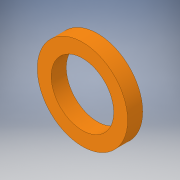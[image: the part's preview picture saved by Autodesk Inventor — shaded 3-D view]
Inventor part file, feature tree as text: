
AUTODESK INVENTOR PART (.ipt)
format: ipt  version: 2017 (Build 210142000, 142)  size: 103,936 bytes
history: native  units: in
note: dims shown in document units (in); Inventor stores cm internally (conversion verified against a paired STEP export)
features: sketch x3, hole x2, extrude x1
ambient origin geometry x8: Origin, YZ Plane, XZ Plane, XY Plane, X Axis, Y Axis, Z Axis, Center Point
bodies: Solid1 (feature_tree)
feature tree (6):
  extrude  "Extrusion1"  Depth=0.125in TaperAngle=0.0deg
  hole  "Hole1"  [1 undecoded]
  hole  "Hole2"  [1 undecoded]
  sketch  "Sketch1"  dims[d0=0.75in d1=0.125in d2=0.0in]
  sketch  "Sketch2"  dims[d3=0.51in d4=0.75in d5=0.375in d6=0.25in d7=0.5635in d8=1.0in d9=0.8108in]
  sketch  "Sketch3"  dims[d10=0.52in d11=0.75in d12=0.375in d13=0.25in d14=0.5635in d15=1.0in d16=0.8108in]
note: 2 required parameter values undecoded (feature->parameter linkage not recoverable at this tier; creation-order binding heuristic only, values carry confidence <= 0.55)
